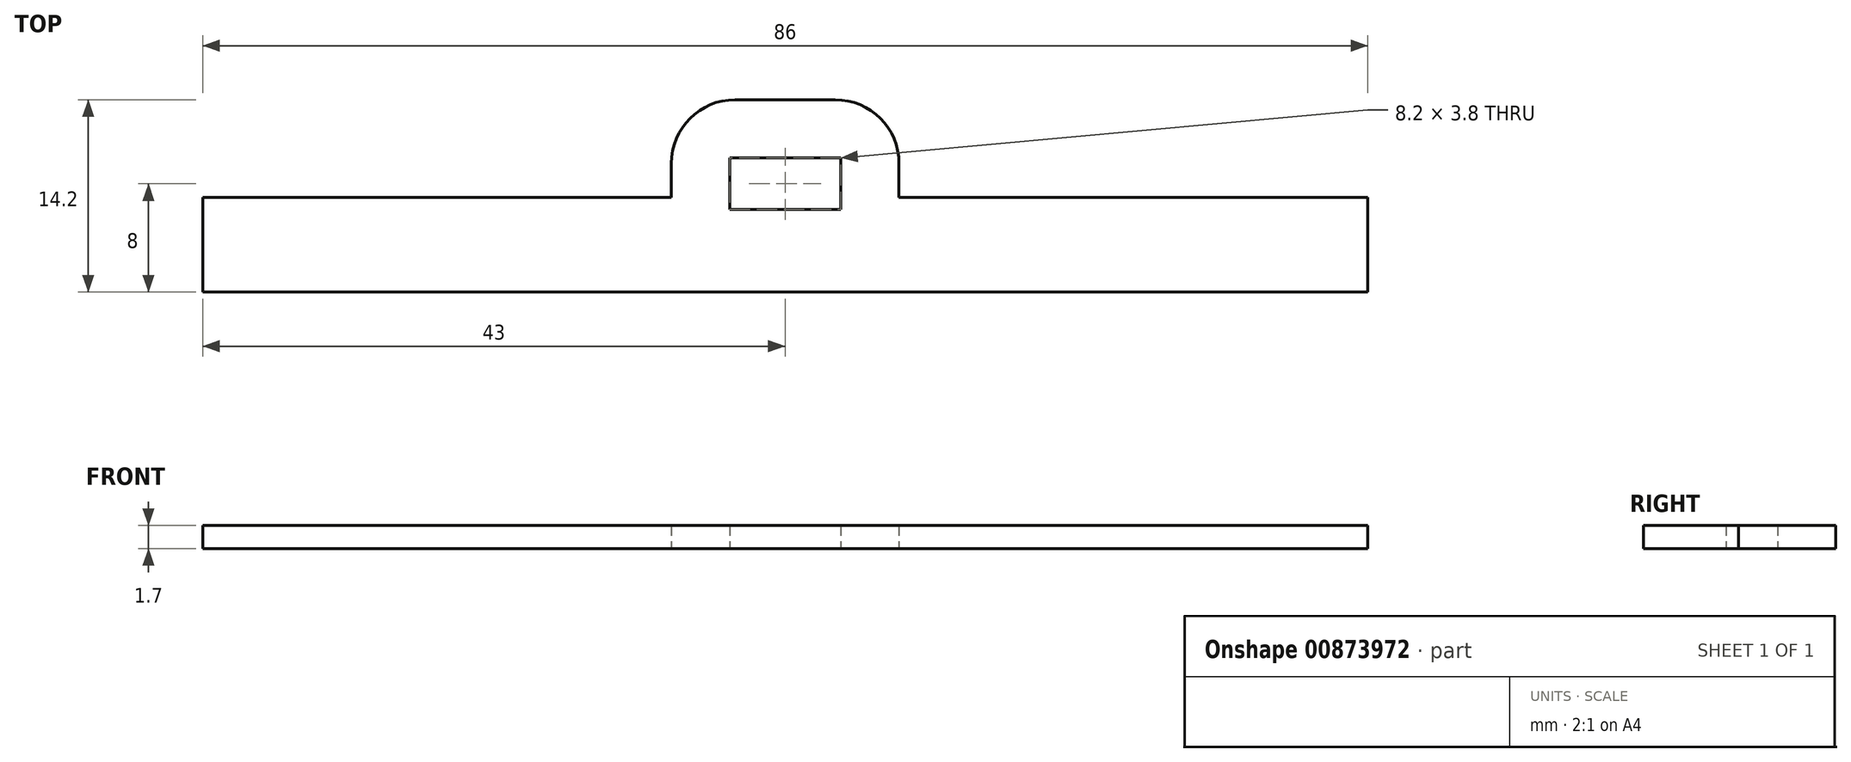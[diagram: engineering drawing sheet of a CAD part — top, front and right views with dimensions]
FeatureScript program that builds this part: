
annotation { "Feature Type Name" : "Feature", "Feature Type Description" : "" }
export const myFeature = defineFeature(function(context is Context, id is Id, definition is map)
    precondition{}
    {
        {
            var Q0;
            Q0=qCreatedBy(makeId("Top.planeOp"),FACE);
            var sketch = newSketch(context, id + "F0", { "sketchPlane" : qUnion([Q0])});
            skLineSegment(sketch, "E0", {"start": v(0, 0) * mm, "end": v(-86, 0) * mm});
            skLineSegment(sketch, "E1", {"start": v(-86, 0) * mm, "end": v(-86, 7) * mm});
            skLineSegment(sketch, "E2", {"start": v(-86, 7) * mm, "end": v(0, 7) * mm});
            skLineSegment(sketch, "E3", {"start": v(0, 7) * mm, "end": v(0, 0) * mm});
            skLineSegment(sketch, "E4", {"start": v(-43, 0) * mm, "end": v(-43, 6.1) * mm});
            skLineSegment(sketch, "E5", {"start": v(-43, 6.1) * mm, "end": v(-47.1, 6.1) * mm});
            skLineSegment(sketch, "E6", {"start": v(-43, 6.1) * mm, "end": v(-38.9, 6.1) * mm});
            skLineSegment(sketch, "E7", {"start": v(-38.9, 6.1) * mm, "end": v(-38.9, 9.9) * mm});
            skLineSegment(sketch, "E8", {"start": v(-38.9, 9.9) * mm, "end": v(-47.1, 9.9) * mm});
            skLineSegment(sketch, "E9", {"start": v(-47.1, 9.9) * mm, "end": v(-47.1, 6.1) * mm});
            skLineSegment(sketch, "E10", {"start": v(-38.9, 9.9) * mm, "end": v(-38.9, 14.2) * mm});
            skLineSegment(sketch, "E11", {"start": v(-38.9, 14.2) * mm, "end": v(-47.1, 14.2) * mm});
            skLineSegment(sketch, "E12", {"start": v(-47.1, 14.2) * mm, "end": v(-47.1, 9.9) * mm});
            skLineSegment(sketch, "E13", {"start": v(-47.1, 14.2) * mm, "end": v(-51.4, 14.2) * mm});
            skLineSegment(sketch, "E14", {"start": v(-51.4, 14.2) * mm, "end": v(-51.4, 7) * mm});
            skLineSegment(sketch, "E15", {"start": v(-38.9, 14.2) * mm, "end": v(-34.6, 14.2) * mm});
            skLineSegment(sketch, "E16", {"start": v(-34.6, 14.2) * mm, "end": v(-34.6, 7) * mm});
            skSolve(sketch);
        }
        {
            var Q0;
            {var subQ0=sQuery(id+"F0.wireOp",EDGE,"E3");Q0=makeQuery(id+"F0.imprint","IMPRINT",FACE,{"disambiguationData":[TD([[makeQuery(id+"F0.imprint","IMPRINT",EDGE,{"derivedFrom":subQ0}),-1.0]])]});}
            var Q1;
            {var subQ0=sQuery(id+"F0.wireOp",EDGE,"E10");Q1=makeQuery(id+"F0.imprint","IMPRINT",FACE,{"disambiguationData":[TD([[makeQuery(id+"F0.imprint","IMPRINT",EDGE,{"derivedFrom":subQ0}),-1.0]])]});}
            var Q2;
            Q2=makeQuery(id+"F0.imprint","IMPRINT",FACE,{"disambiguationData":[TD([[makeQuery(id+"F0.imprint","IMPRINT",EDGE,{"derivedFrom":sQuery(id+"F0.wireOp",EDGE,"E8")}),-1.0]])]});
            var Q3;
            {var subQ0=sQuery(id+"F0.wireOp",EDGE,"E12");Q3=makeQuery(id+"F0.imprint","IMPRINT",FACE,{"disambiguationData":[TD([[makeQuery(id+"F0.imprint","IMPRINT",EDGE,{"derivedFrom":subQ0}),-1.0]])]});}
            var Q4;
            {var subQ4=sQuery(id+"F0.wireOp",EDGE,"E1");Q4=makeQuery(id+"F0.imprint","IMPRINT",FACE,{"disambiguationData":[TD([[makeQuery(id+"F0.imprint","IMPRINT",EDGE,{"derivedFrom":subQ4}),-1.0]])]});}
            extrude(context, id + "F1", {"entities" : qUnion([Q0, Q1, Q2, Q3, Q4]), "flatOperationType" : FlatOperationType.REMOVE, "depth" : 1.7 * mm, "offsetDistance" : 25 * mm, "domain" : OperationDomain.MODEL});
        }
        {
            var Q0;
            Q0=makeQuery(id+"F1.opExtrude","SWEPT_EDGE",EDGE,{"disambiguationData":[OSD([sQuery(id+"F0.wireOp",EDGE,"E15"),sQuery(id+"F0.wireOp",EDGE,"E16")])]});
            var Q1;
            Q1=makeQuery(id+"F1.opExtrude","SWEPT_EDGE",EDGE,{"disambiguationData":[OSD([sQuery(id+"F0.wireOp",EDGE,"E13"),sQuery(id+"F0.wireOp",EDGE,"E14")])]});
            fillet(context, id + "F2", {"entities" : qUnion([Q0, Q1]), "radius" : 4.7 * mm, "tangentPropagation" : true, "allowEdgeOverflow" : false});
        }
    });
